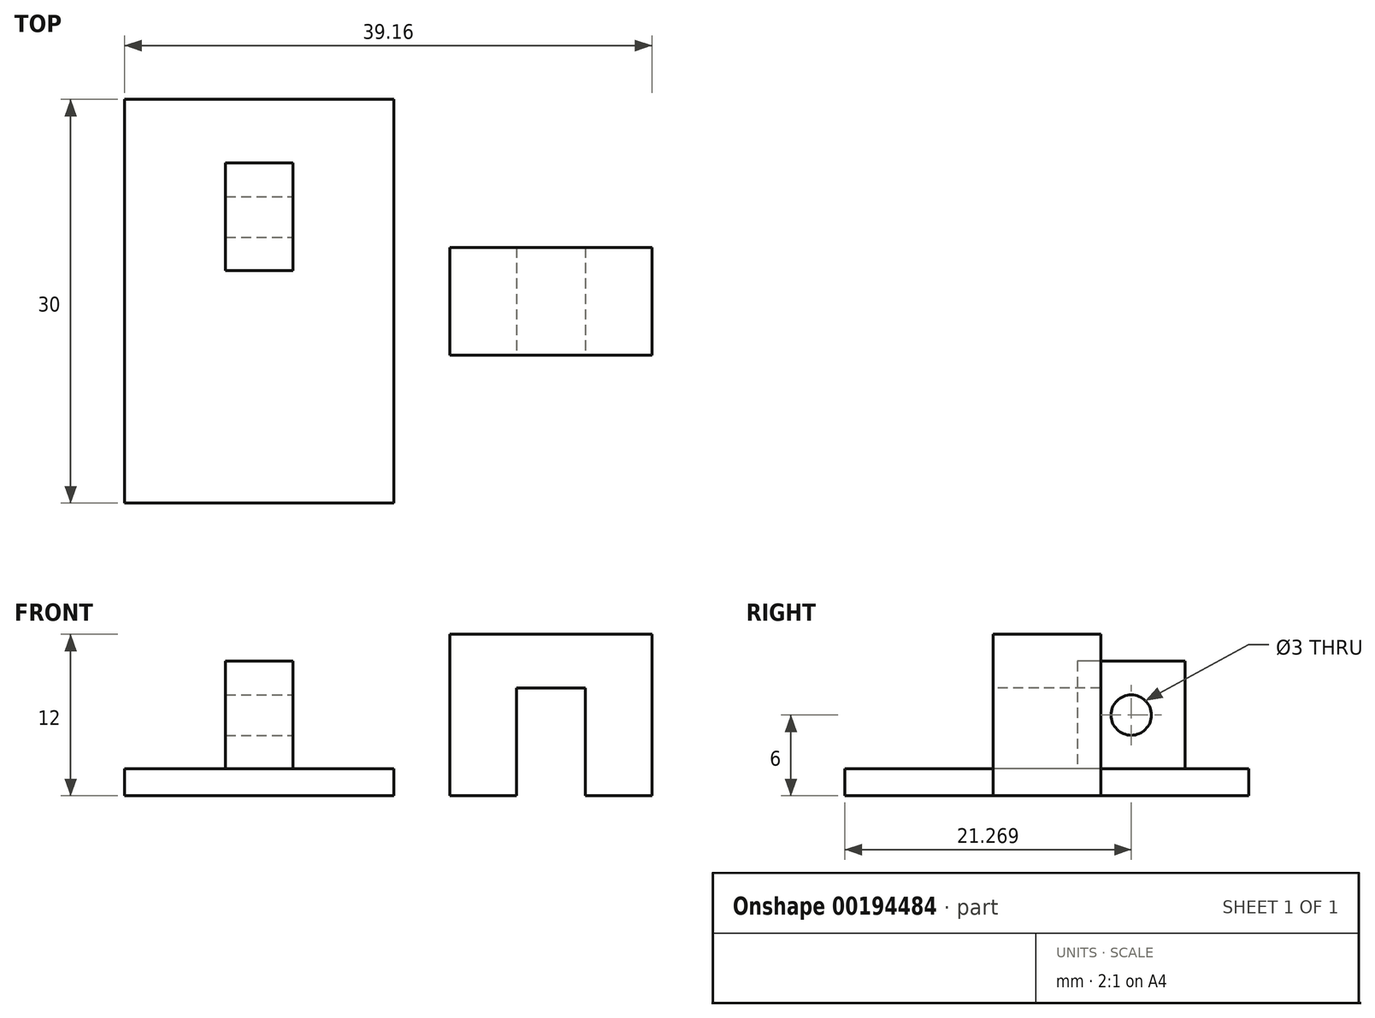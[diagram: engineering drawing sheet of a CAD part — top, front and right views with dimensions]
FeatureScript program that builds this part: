
annotation { "Feature Type Name" : "Feature", "Feature Type Description" : "" }
export const myFeature = defineFeature(function(context is Context, id is Id, definition is map)
    precondition{}
    {
        {
            var Q0;
            Q0=qCreatedBy(makeId("Top.planeOp"),FACE);
            var sketch = newSketch(context, id + "F0", { "sketchPlane" : qUnion([Q0])});
            skLineSegment(sketch, "E0.bottom", {"start": v(10, 15) * mm, "end": v(-10, 15) * mm});
            skLineSegment(sketch, "E0.top", {"start": v(10, -15) * mm, "end": v(-10, -15) * mm});
            skLineSegment(sketch, "E0.left", {"start": v(10, 15) * mm, "end": v(10, -15) * mm});
            skLineSegment(sketch, "E0.right", {"start": v(-10, 15) * mm, "end": v(-10, -15) * mm});
            skPoint(sketch, "E0.middle", {"position": v(0, 0) * mm});
            skSolve(sketch);
        }
        {
            var Q0;
            Q0 = qSketchRegion(id + "F0", true);
            extrude(context, id + "F1", {"entities" : qUnion([Q0]), "depth" : 2 * mm});
        }
        {
            var Q0;
            Q0=makeQuery(id+"F1.opExtrude","CAP_FACE",FACE,{"disambiguationData":[OSD([sQuery(id+"F0.wireOp",EDGE,"E0.bottom"),sQuery(id+"F0.wireOp",EDGE,"E0.top"),sQuery(id+"F0.wireOp",EDGE,"E0.left"),sQuery(id+"F0.wireOp",EDGE,"E0.right")])],"isStart":false});
            var sketch = newSketch(context, id + "F2", { "sketchPlane" : qUnion([Q0])});
            skLineSegment(sketch, "E1.bottom", {"start": v(2.5, 10.27) * mm, "end": v(-2.5, 10.27) * mm});
            skLineSegment(sketch, "E1.top", {"start": v(2.5, 2.27) * mm, "end": v(-2.5, 2.27) * mm});
            skLineSegment(sketch, "E1.left", {"start": v(2.5, 10.27) * mm, "end": v(2.5, 2.27) * mm});
            skLineSegment(sketch, "E1.right", {"start": v(-2.5, 10.27) * mm, "end": v(-2.5, 2.27) * mm});
            skPoint(sketch, "E1.middle", {"position": v(0, 6.27) * mm});
            skLineSegment(sketch, "E2.bottom", {"start": v(18.7, 10.27) * mm, "end": v(13.7, 10.27) * mm});
            skLineSegment(sketch, "E2.top", {"start": v(18.7, 2.27) * mm, "end": v(13.7, 2.27) * mm});
            skLineSegment(sketch, "E2.left", {"start": v(18.7, 10.27) * mm, "end": v(18.7, 2.27) * mm});
            skLineSegment(sketch, "E2.right", {"start": v(13.7, 10.27) * mm, "end": v(13.7, 2.27) * mm});
            skPoint(sketch, "E2.middle", {"position": v(16.2, 6.27) * mm});
            skPoint(sketch, "E2.middle.positionSnap0", {"position": v(2.5, 6.27) * mm});
            skPoint(sketch, "E2.centerSnap0", {"position": v(2.5, 6.27) * mm});
            skSolve(sketch);
        }
        {
            var Q0;
            Q0 = qSketchRegion(id + "F2", true);
            extrude(context, id + "F3", {"entities" : qUnion([Q0]), "operationType" : NewBodyOperationType.ADD, "depth" : 8 * mm});
        }
        {
            var Q0;
            Q0=makeQuery(id+"F3.opExtrude","SWEPT_FACE",FACE,{"disambiguationData":[OSD([sQuery(id+"F2.wireOp",EDGE,"E1.left")])]});
            var sketch = newSketch(context, id + "F4", { "sketchPlane" : qUnion([Q0])});
            skCircle(sketch, "E3", {"center": v(6.27, 6) * mm, "radius": 1.5 * mm});
            skPoint(sketch, "E3.centerSnap0", {"position": v(6.27, 2) * mm});
            skPoint(sketch, "E3.centerSnap1", {"position": v(2.27, 6) * mm});
            skSolve(sketch);
        }
        {
            var Q0;
            Q0 = qSketchRegion(id + "F4", true);
            extrude(context, id + "F5", {"entities" : qUnion([Q0]), "operationType" : NewBodyOperationType.REMOVE, "oppositeDirection" : true, "depth" : 25 * mm, "hasSecondDirection" : true, "secondDirectionOppositeDirection" : false, "secondDirectionDepth" : 25 * mm});
        }
        {
            var Q0;
            Q0=makeQuery(id+"F3.opExtrude","SWEPT_BODY",BODY,{"disambiguationData":[OSD([sQuery(id+"F2.wireOp",EDGE,"E2.bottom"),sQuery(id+"F2.wireOp",EDGE,"E2.top"),sQuery(id+"F2.wireOp",EDGE,"E2.left"),sQuery(id+"F2.wireOp",EDGE,"E2.right")])]});
            transform(context, id + "F6", {"entities" : qUnion([Q0]), "transformType" : TransformType.TRANSLATION_3D, "dx" : 0 * mm, "dy" : 0 * mm, "dz" : 0 * mm, "makeCopy" : true});
        }
        {
            var Q0;
            Q0=makeQuery(id+"F3.opExtrude","SWEPT_BODY",BODY,{"disambiguationData":[OSD([sQuery(id+"F2.wireOp",EDGE,"E2.bottom"),sQuery(id+"F2.wireOp",EDGE,"E2.top"),sQuery(id+"F2.wireOp",EDGE,"E2.left"),sQuery(id+"F2.wireOp",EDGE,"E2.right")])]});
            deleteBodies(context, id + "F7", {"entities" : qUnion([Q0])});
        }
        {
            var Q0;
            Q0=makeQuery(id+"F6.opPattern","COPY",BODY,{"derivedFrom":makeQuery(id+"F3.opExtrude","SWEPT_BODY",BODY,{"disambiguationData":[OSD([sQuery(id+"F2.wireOp",EDGE,"E2.bottom"),sQuery(id+"F2.wireOp",EDGE,"E2.top"),sQuery(id+"F2.wireOp",EDGE,"E2.left"),sQuery(id+"F2.wireOp",EDGE,"E2.right")])]}),"instanceName":"1"});
            deleteBodies(context, id + "F8", {"entities" : qUnion([Q0])});
        }
        {
            var Q0;
            Q0=qCreatedBy(makeId("Top.planeOp"),FACE);
            var sketch = newSketch(context, id + "F9", { "sketchPlane" : qUnion([Q0])});
            skLineSegment(sketch, "E4.bottom", {"start": v(29.16, 4) * mm, "end": v(14.16, 4) * mm});
            skLineSegment(sketch, "E4.top", {"start": v(29.16, -4) * mm, "end": v(14.16, -4) * mm});
            skLineSegment(sketch, "E4.left", {"start": v(29.16, 4) * mm, "end": v(29.16, -4) * mm});
            skLineSegment(sketch, "E4.right", {"start": v(14.16, 4) * mm, "end": v(14.16, -4) * mm});
            skPoint(sketch, "E4.middle", {"position": v(21.66, 0) * mm});
            skSolve(sketch);
        }
        {
            var Q0;
            Q0 = qSketchRegion(id + "F9", true);
            extrude(context, id + "F10", {"entities" : qUnion([Q0]), "depth" : 12 * mm});
        }
        {
            var Q0;
            Q0=makeQuery(id+"F10.opExtrude","SWEPT_FACE",FACE,{"disambiguationData":[OSD([sQuery(id+"F9.wireOp",EDGE,"E4.top")])]});
            var sketch = newSketch(context, id + "F11", { "sketchPlane" : qUnion([Q0])});
            skLineSegment(sketch, "E5.bottom", {"start": v(24.21, 8) * mm, "end": v(19.11, 8) * mm});
            skLineSegment(sketch, "E5.top", {"start": v(24.21, 0) * mm, "end": v(19.11, 0) * mm});
            skLineSegment(sketch, "E5.left", {"start": v(24.21, 8) * mm, "end": v(24.21, 0) * mm});
            skLineSegment(sketch, "E5.right", {"start": v(19.11, 8) * mm, "end": v(19.11, 0) * mm});
            skPoint(sketch, "E5.middle", {"position": v(21.66, 6) * mm});
            skPoint(sketch, "E5.middle.positionSnap0", {"position": v(21.66, 0) * mm});
            skPoint(sketch, "E5.middle.positionSnap1", {"position": v(14.16, 6) * mm});
            skPoint(sketch, "E5.centerSnap0", {"position": v(21.66, 0) * mm});
            skPoint(sketch, "E5.centerSnap1", {"position": v(14.16, 6) * mm});
            skSolve(sketch);
        }
        {
            var Q0;
            Q0 = qSketchRegion(id + "F11", true);
            extrude(context, id + "F12", {"entities" : qUnion([Q0]), "operationType" : NewBodyOperationType.REMOVE, "oppositeDirection" : true, "depth" : 25 * mm, "hasSecondDirection" : true, "secondDirectionOppositeDirection" : false, "secondDirectionDepth" : 25 * mm});
        }
    });
